# Revit family: LOROWERK 21526-125X
name_source: partatom
category: Plumbing Fixtures
revit_build: Autodesk Revit 2017 (Build: 20160225_1515(x64)
units: mm (PartAtom-declared; Revit-internal decimal feet)

## family parameters
Always vertical = Yes
Cut with Voids When Loaded = No
Part Type = Normal
Room Calculation Point = No
Round Connector Dimension = Use Diameter
Shared = No
Work Plane-Based = No

## types (1)
- LOROWERK 21526-125X
    Abdichtvarianten = mit Klemmflansch (Pressdichtungsflansch)
    Abflussstutzen Ausführung = waagerecht
    Ablaufanschluss = seitlich
    Anschluss an GLT, GA = No
    BIM = https://media.stage.bim.site
    CONNECTOR0_DIAMETER_dZ_0r = 125 mm
    CONNECTOR0_dZ_00 = 53 mm
    CONNECTOR0_dZ_01 = 53 mm
    CONNECTOR0_ref_dZ = 53 mm
    CONNECTOR1_DIAMETER_dNBN0_0r = 125 mm
    CONNECTOR1_dNBN0_00 = 46 mm
    CONNECTOR1_dNBN0_01 = 291 mm
    CONNECTOR1_ref_dNBN0 = 46 mm
    CONNECTOR1_ref_dNBN1 = 108 mm
    DATANORM = 21526.125X
    Description = LORO-DRAINLET DL Flachdachabläufe, Kompletteinheiten, zweiteilig
    Einbaubreite [m] = 0.33
    Einbauhöhe [m] = 0.364
    Einbautiefe [m] = 0.453
    Elektrischer Anschluss = No
    Feuerwiderstandsklasse nachrüstbar 6 = No
    GTIN = 4038088085905
    Gehäuseanschlussarten = Ablauf-Punktförmig
    Geruchsverschluss = ohne Geruchverschluss
    HAN = 21526.125X
    Ist System = No
    Ist Zubehör = No
    Komplettartikel (Einteilig) aus Kombination (Mehrteileausführung) Ablaufgrundkörper und Aufsatzstück = Yes
    Manufacturer = LOROWERK K.H. Vahlbrauk GmbH & Co. KG
    Nenndrucksystem = PN
    Nennmaß = 125
    Nennweitensystem = DN
    Potenzialausgleich (Erdungsanschluss) vorhanden = No
    Produktbezeichnung = LORO-DRAINLET DL Flachdachabläufe, Kompletteinheiten, zweiteilig
    Produktklassifikation = Flachdachablauf
    Produktname = LORO-DL Ablauf, Edelstahl, Klemmflansch, seitl., 2-tlg., WD u. Heizung, DN125
    Produktvideo = https://media.stage.bim.site
    Sperrwasserhöhe [m] = 0.035
    Typ = Dachablauf
    Type Name = LORO-DL Ablauf, Edelstahl, Klemmflansch, seitl., 2-tlg., WD u. Heizung, DN125
    VDIBSN = 0020040000020010000010010020010000000030020000002100000001
    Variante/Varianten-Art/Zubehörbezeichnung = mit Begleitheizung
    Werkstoff des Ablaufkörpers = nicht rostender Stahl
    mit Blätter-/Kiesfang = Yes
    mit Schallentkopplung = No

## geometry (parser evidence)
native form markers: Blend x2, Sweep x3
no freeform markers — native parametric forms only
